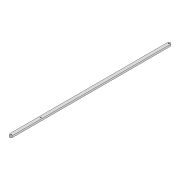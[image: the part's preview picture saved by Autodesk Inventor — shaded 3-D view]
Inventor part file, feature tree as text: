
AUTODESK INVENTOR PART (.ipt)
format: ipt  version: 2022 (Build 260153000, 153)  size: 88,064 bytes
history: native  units: mm
features: extrude x1, sketch x1
ambient origin geometry x8: Origin, YZ Plane, XZ Plane, XY Plane, X Axis, Y Axis, Z Axis, Center Point
bodies: Solid1 (feature_tree)
feature tree (2):
  extrude  "Extrusion1"  Depth=8.0mm
  sketch  "Sketch1"  dims[d0=411.151mm d1=8.0mm d2=3.0mm d3=3.0mm d4=4.5mm d5=0.0mm d6=3.0mm d7=334.103mm]
